# Revit family: ITK Проходной адаптер ST-ST_SM-MM_UPC_Simplex
name_source: partatom
category: Обобщенные модели
units: mm (PartAtom-declared; Revit-internal decimal feet)

## family parameters
Всегда вертикально = Да
Может служить основой для арматурных стержней = Нет
На основе рабочей плоскости = Нет
Общий = Нет
При загрузке вырезать с полостями = Нет
Размер круглого соединителя = Использовать диаметр
Тип детали = Нормальный
Точка расчета площади = Нет

## types (1)
- FC1-STUSTU1C-SM
    ADSK_URL страницы изделия = https://www.itk-group.ru
    ADSK_Версия Revit = 2019
    ADSK_Версия семейства = 1.0
    ADSK_Группирование = I. ЩИТЫ И ПУЛЬТЫ
    ADSK_Единица измерения = шт
    ADSK_Завод-изготовитель = IEK
    ADSK_Код изделия = FC1-STUSTU1C-SM
    ADSK_Масса = 0
    ADSK_Материал наименование = Металл
    ADSK_Наименование = ITK Проходной адаптер ST-ST, (SM/MM), UPC, (Simplex)
    IEK_URL = https://www.itk-group.ru
    IEK_Описание = Качественное, надежное соединение для передачи сигнала.
Большой ресурс включений - 500.
Высококачественный материал продукции.
Большой диапазон температур от -40°C до +75°C.
    IEK_Цена за единицу = 33.67
    KSI_CMa_Строительные материалы = 10.1.01.01
    KSI_CPr_Строительные изделия = 61.1.03.04
    URL = https://www.iek.ru
    Изготовитель = ITK
    Материал = Пластик желтый
    Ширина = 38 мм
